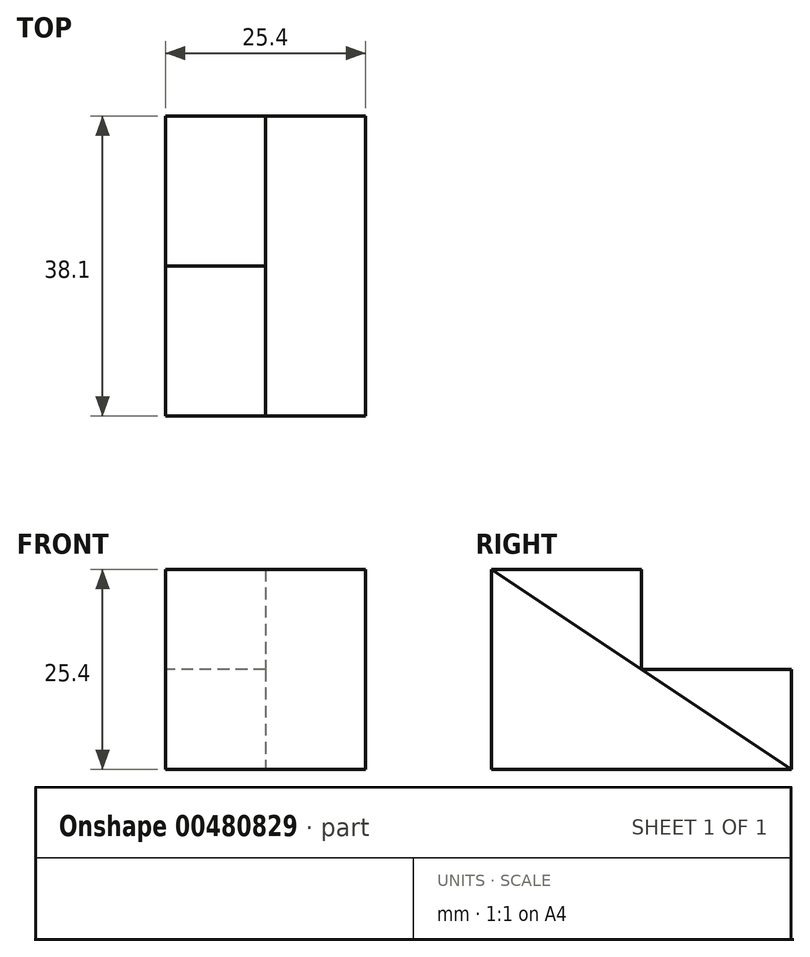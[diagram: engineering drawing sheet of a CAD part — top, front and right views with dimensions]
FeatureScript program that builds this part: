
annotation { "Feature Type Name" : "Feature", "Feature Type Description" : "" }
export const myFeature = defineFeature(function(context is Context, id is Id, definition is map)
    precondition{}
    {
        {
            var Q0;
            Q0=qCreatedBy(makeId("Right.planeOp"),FACE);
            var sketch = newSketch(context, id + "F0", { "sketchPlane" : qUnion([Q0])});
            skLineSegment(sketch, "E0", {"start": v(-38.1, 25.4) * mm, "end": v(-38.1, 0) * mm});
            skLineSegment(sketch, "E1", {"start": v(-38.1, 0) * mm, "end": v(0, 0) * mm});
            skLineSegment(sketch, "E2", {"start": v(0, 0) * mm, "end": v(-38.1, 25.4) * mm});
            skSolve(sketch);
        }
        {
            var Q0;
            Q0=qCreatedBy(makeId("Right.planeOp"),FACE);
            var sketch = newSketch(context, id + "F1", { "sketchPlane" : qUnion([Q0])});
            skLineSegment(sketch, "E3", {"start": v(-38.1, 25.4) * mm, "end": v(-19.05, 25.4) * mm});
            skLineSegment(sketch, "E4", {"start": v(-19.05, 25.4) * mm, "end": v(-19.05, 12.7) * mm});
            skLineSegment(sketch, "E5", {"start": v(-19.05, 12.7) * mm, "end": v(0, 12.7) * mm});
            skLineSegment(sketch, "E6", {"start": v(0, 12.7) * mm, "end": v(0, 0) * mm});
            skLineSegment(sketch, "E7", {"start": v(-38.1, 25.4) * mm, "end": v(0, 0) * mm});
            skSolve(sketch);
        }
        {
            var Q0;
            Q0=makeQuery(id+"F0.imprint","IMPRINT",FACE,{"disambiguationData":[TD([[makeQuery(id+"F0.imprint","IMPRINT",EDGE,{"derivedFrom":sQuery(id+"F0.wireOp",EDGE,"E0")}),1.0]])]});
            extrude(context, id + "F2", {"entities" : qUnion([Q0]), "depth" : 25.4 * mm});
        }
        {
            var Q0;
            {var subQ0=sQuery(id+"F1.wireOp",EDGE,"E3");Q0=makeQuery(id+"F1.imprint","IMPRINT",FACE,{"disambiguationData":[TD([[makeQuery(id+"F1.imprint","IMPRINT",EDGE,{"derivedFrom":subQ0}),-1.0]])]});}
            var Q1;
            {var subQ0=sQuery(id+"F1.wireOp",EDGE,"E5");Q1=makeQuery(id+"F1.imprint","IMPRINT",FACE,{"disambiguationData":[TD([[makeQuery(id+"F1.imprint","IMPRINT",EDGE,{"derivedFrom":subQ0}),-1.0]])]});}
            extrude(context, id + "F3", {"entities" : qUnion([Q0, Q1]), "operationType" : NewBodyOperationType.ADD, "depth" : 12.7 * mm});
        }
    });
